# Revit family: Chic Lounge
name_source: partatom
category: Furniture
units: mm (PartAtom-declared; Revit-internal decimal feet)

## family parameters
Always vertical = Yes
Cut with Voids When Loaded = No
OmniClass Number = 23.40.20.00
OmniClass Title = General Furniture and Specialties
Room Calculation Point = No
Shared = No
Work Plane-Based = No

## types (6) — shared parameters
Default Elevation = 0' - 0"
Manufacturer = AIS Inc
Product = CHIC LOUNGE
URL = https://www.ais-inc.com

## per-type parameters (varying)
| type | Description | LCHC1 | LCHC1C | LCHC2 | LCHC2C | LCHC3 | LCHC3C | Model |
| LCHC1-Metal Legs | 33"Wx30.5"Dx29"H Chic club chair, metal legs | Yes | No | No | No | No | No | LCHC1 |
| LCHC1C-Configurable | 33"Wx30.5"Dx29"H Chic club chair, metal legs, Configurable | No | Yes | No | No | No | No | LCHC1C |
| LCHC2C-Configurable | 53"Wx30.5"Dx29"H Chic 2-Seater, metal legs, Configurable | No | No | No | Yes | No | No | LCHC2C |
| LCHC2-Metal Legs | 53"Wx30.5"Dx29"H Chic 2-Seater, metal legs | No | No | Yes | No | No | No | LCHC2 |
| LCHC3-Metal Legs | 73"Wx30.5"Dx29"H Chic 3-Seater, metal legs | No | No | No | No | Yes | No | LCHC3 |
| LCHC3C-Configurable | 73"Wx30.5"Dx29"H Chic 3-Seater, metal legs, Configurable | No | No | No | No | No | Yes | LCHC3C |

## geometry (parser evidence)
native form markers: Sweep x3
no freeform markers — native parametric forms only
